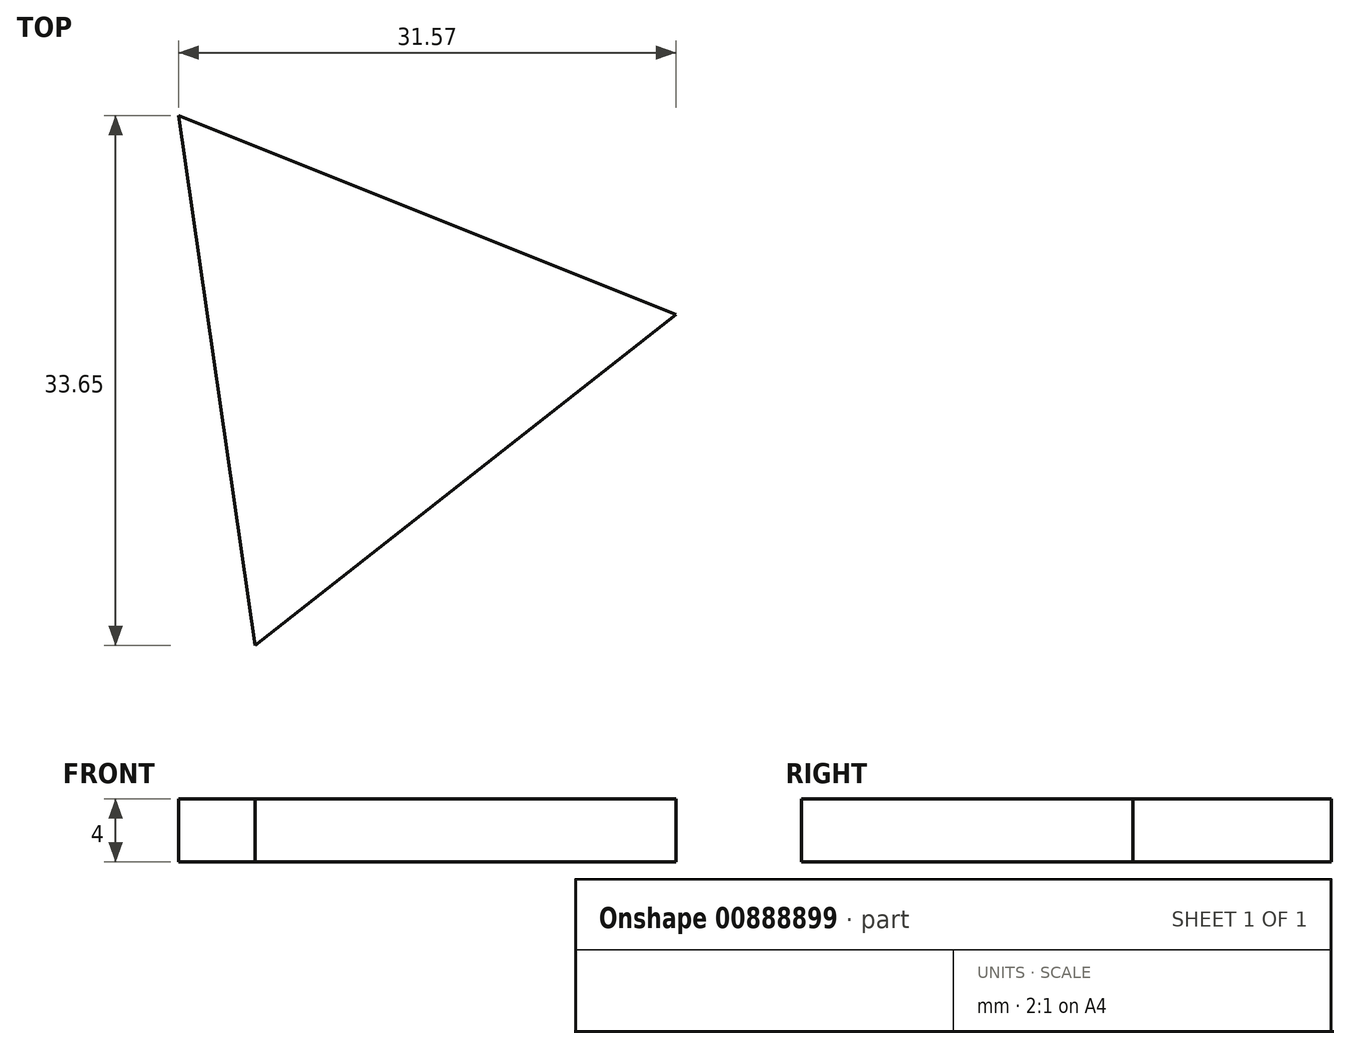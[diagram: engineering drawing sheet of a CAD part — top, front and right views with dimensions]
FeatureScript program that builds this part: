
annotation { "Feature Type Name" : "Feature", "Feature Type Description" : "" }
export const myFeature = defineFeature(function(context is Context, id is Id, definition is map)
    precondition{}
    {
        {
            var Q0;
            Q0=qCreatedBy(makeId("Top.planeOp"),FACE);
            var sketch = newSketch(context, id + "F0", { "sketchPlane" : qUnion([Q0])});
            skCircle(sketch, "E0.cCircle", {"center": v(-7.33, 7.71) * mm, "radius": 9.81 * mm, "construction": true});
            skLineSegment(sketch, "E0.0", {"start": v(12.1, 10.51) * mm, "end": v(-14.62, -10.51) * mm});
            skLineSegment(sketch, "E0.1", {"start": v(-14.62, -10.51) * mm, "end": v(-19.47, 23.14) * mm});
            skLineSegment(sketch, "E0.2", {"start": v(-19.47, 23.14) * mm, "end": v(12.1, 10.51) * mm});
            skPoint(sketch, "E0.0.midPoint", {"position": v(-1.26, 0) * mm});
            skSolve(sketch);
        }
        {
            var Q0;
            Q0 = qSketchRegion(id + "F0", true);
            extrude(context, id + "F1", {"entities" : qUnion([Q0]), "depth" : 4 * mm, "offsetDistance" : 25.4 * mm});
        }
    });
